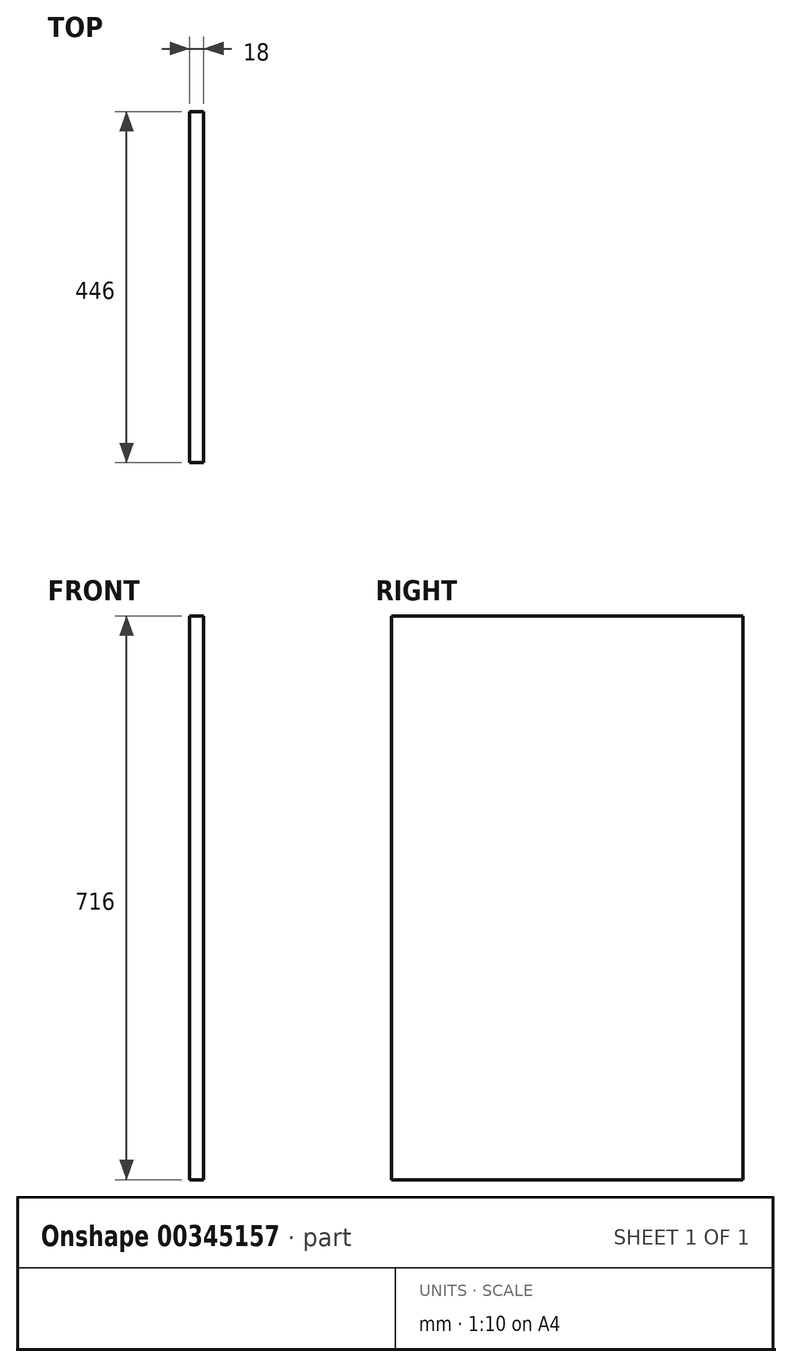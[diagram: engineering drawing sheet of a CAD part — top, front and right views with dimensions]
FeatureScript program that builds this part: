
annotation { "Feature Type Name" : "Feature", "Feature Type Description" : "" }
export const myFeature = defineFeature(function(context is Context, id is Id, definition is map)
    precondition{}
    {
        {
            var Q0;
            Q0=qCreatedBy(makeId("Right.planeOp"),FACE);
            var sketch = newSketch(context, id + "F0", { "sketchPlane" : qUnion([Q0])});
            skLineSegment(sketch, "E0.bottom", {"start": v(0, 0) * mm, "end": v(-47.1, 0) * mm});
            skLineSegment(sketch, "E0.top", {"start": v(0, 38.53) * mm, "end": v(-47.1, 38.53) * mm});
            skLineSegment(sketch, "E0.left", {"start": v(0, 0) * mm, "end": v(0, 38.53) * mm});
            skLineSegment(sketch, "E0.right", {"start": v(-47.1, 0) * mm, "end": v(-47.1, 38.53) * mm});
            skSolve(sketch);
        }
        {
            var Q0;
            Q0=makeQuery(id+"F0.imprint","IMPRINT",FACE,{"disambiguationData":[TD([[makeQuery(id+"F0.imprint","IMPRINT",EDGE,{"derivedFrom":sQuery(id+"F0.wireOp",EDGE,"E0.bottom")}),-1.0]])]});
            extrude(context, id + "F1", {"entities" : qUnion([Q0]), "oppositeDirection" : true, "depth" : 18 * mm});
        }
        {
            var Q0;
            Q0=makeQuery(id+"F1.opExtrude","SWEPT_FACE",FACE,{"disambiguationData":[OSD([sQuery(id+"F0.wireOp",EDGE,"E0.left")])]});
            extrude(context, id + "F2", {"entities" : qUnion([Q0]), "operationType" : NewBodyOperationType.ADD, "oppositeDirection" : true, "depth" : 446 * mm});
        }
        {
            var Q0;
            {var subQ0=sQuery(id+"F0.wireOp",EDGE,"E0.bottom");Q0=makeQuery(id+"F2.boolean.opBoolean","MERGE",FACE,{"derivedFrom":[makeQuery(id+"F1.opExtrude","SWEPT_FACE",FACE,{"disambiguationData":[OSD([subQ0])]}),makeQuery(id+"F2.opExtrude","SWEPT_FACE",FACE,{"disambiguationData":[OSD([subQ0,sQuery(id+"F0.wireOp",EDGE,"E0.left")])]})]});}
            extrude(context, id + "F3", {"entities" : qUnion([Q0]), "operationType" : NewBodyOperationType.ADD, "oppositeDirection" : true, "depth" : 716 * mm});
        }
    });
